# Revit family: Camera-Security-Panasonic-Super_Dynamic-Vandal_Resistant-Waterproof-Dome-Network-S2531LNSeriesX
name_source: partatom
category: Security Devices
revit_build: Autodesk Revit 2016 (Build: 20150714_1515(x64)
units: mm (PartAtom-declared; Revit-internal decimal feet)

## family parameters
Cut with Voids When Loaded = No
Host = Face
Maintain Annotation Orientation = No
OmniClass Number = 23.85.10.14.11
OmniClass Title = Cameras
Part Type = Normal
Room Calculation Point = No
Round Connector Dimension = Use Diameter
Shared = No

## types (3) — shared parameters
Alarm Input Or Output Specification = ALARM IN 1 (DAY/NIGHT IN, Auto time adjustment) (x1),ALARM IN 2 (ALARM OUT) (x1), ALARM IN 3 (AUX OUT) (x1)
Audio In = Yes
Audio Out = Yes
Communication Ports = 10Base-T / 100Base-TX, RJ45 connector
Day Or Night = Yes
Diameter = 6.457 "
Equipment Abbreviation = SC
Family Version = 1.0.0
Has POE = Yes
Height = 5.472 "
IP Or Analog = IP
Indoor Or Outdoor = Outdoor
Manufacturer = Panasonic
Model Disclaimer = Contact Panasonic for more information
Mounting Positions = Surface Mount
Operational Temperature = 40°F - 122°F
Pan Max = 180.00°
Pan Min = -180.00°
Panning Range = -180 to +180
Power Active = 9.0 W
Product Documentation Link = http://ssbu-t.psn-web.net
Product Material = Paint - Panasonic - Light Gray
Product Page URL = http://security.panasonic.com
Provide Feedback = https://www.surveymonkey.com
Regulatory Compliance = UL UL60950-1, C-UL CAN/CSA C22.2 No.60950-1, CE, IEC60950-1 FCC Part15 ClassA, ICES003 ClassA, EN55022 ClassB, EN55024
Shock Resistance = Compliant with 50J IEC60068-2-75, IK10 (IEC 62262)
Storage Temperature = 40°F - 122°F
Tilt Max = 85.00°
Tilt Min = -30.00°
Tilting Range = -30 to +85
URL = http://security.panasonic.com
Vandal Resistant = Yes
Voltage DC = 12 V
Water and Dust Resistance = IP66, IEC60529 measuring standard compatible, Type 4X(UL50), NEMA 4X compliant
Wide Dynamic Range = Yes
Yaw Max = 100.00°
Yaw Min = -100.00°
Yawing Range = -100 to +100
z Base Height = 3.622 "
z Base Radius = 3.228 "
z Ceiling Mount Bottom Offset = -3.102 "
z Const Pan Handle Length = 19.488 "
z Const Tilt Base Length = 9.843 "
z Const Tilt Base2 Length = 19.685 "
z Const Tilt Handle Length = 11.811 "
z Const Yaw Base Length = 10.236 "
z Const Yaw Base2 Length = 17.323 "
z Const Yaw Handle Length = 9.252 "
z Dome Radius = 1.85 "
z Half Height of LowerBase = 1.561 "
z Has CW63xS Mount Bracket = No
z Has Ceiling Mount Bracket = No
z Has Wall Mount Bracket = No
z Level Offset = 19.685 "
zero-valued in all types: Default Elevation, z Zero

## per-type parameters (varying)
| type | Angle Of View | Date Last Modified | Description | HFOV Max 169 | HFOV Max 43 | HFOV Min 169 | HFOV Min 43 | Minimum Illumination | Operational Humidity | Part Description | VFOV Max 169 | VFOV Max 43 | VFOV Min 169 | VFOV Min 43 | z Camera Resolution Type | z VV Viewpoint Depth Max | z VV Viewpoint Depth Min |
| WV-S2531LN | 108 | 2016/10/31 | Security Camera, Fixed Dome, Network, Super Dynamic Vandal Resistant  Weatherproof,FullHD | 108.00° | 90.00° | 30.00° | 25.00° | 0.012 lx | 10% to 90% (no condensation) | Security Camera, Fixed Dome, Network, Super Dynamic Vandal Resistant  Weatherproof,FullHD | 58.00° | 65.00° | 17.00° | 19.00° | 1 | 1.154 " | 0.823 " |
| WV-S2511LN | 108 | 2016/10/31 | Security Camera, Fixed Dome, Network, Super Dynamic  Vandal Resistant  Weatherproof,HD | 108.00° | 90.00° | 30.00° | 25.00° | 0.008 lx | 10% to 90% (no condensation) | Security Camera, Fixed Dome, Network, Super Dynamic  Vandal Resistant  Weatherproof,HD | 58.00° | 65.00° | 17.00° | 19.00° | 2 | 1.154 " | 0.823 " |
| WV-S2531LTN | 34 | 2017/05/31 | Security Camera, Fixed Dome, Network, Super Dynamic Vandal Resistant,Weatherproof,FullHD | 34.00° | 28.00° | 14.00° | 12.00° | 0.015 lx | 10% to 100% (no condensation) | Security Camera, Fixed Dome, Network, Super Dynamic Vandal Resistant,Weatherproof,FullHD | 19.00° | 21.00° | 8.00° | 9.00° | 1 | 1.135 " | 0.803 " |

note: column(s) folded — value = type name in every type: Model, Part Number

## geometry (parser evidence)
native form markers: Sweep x6
no freeform markers — native parametric forms only
